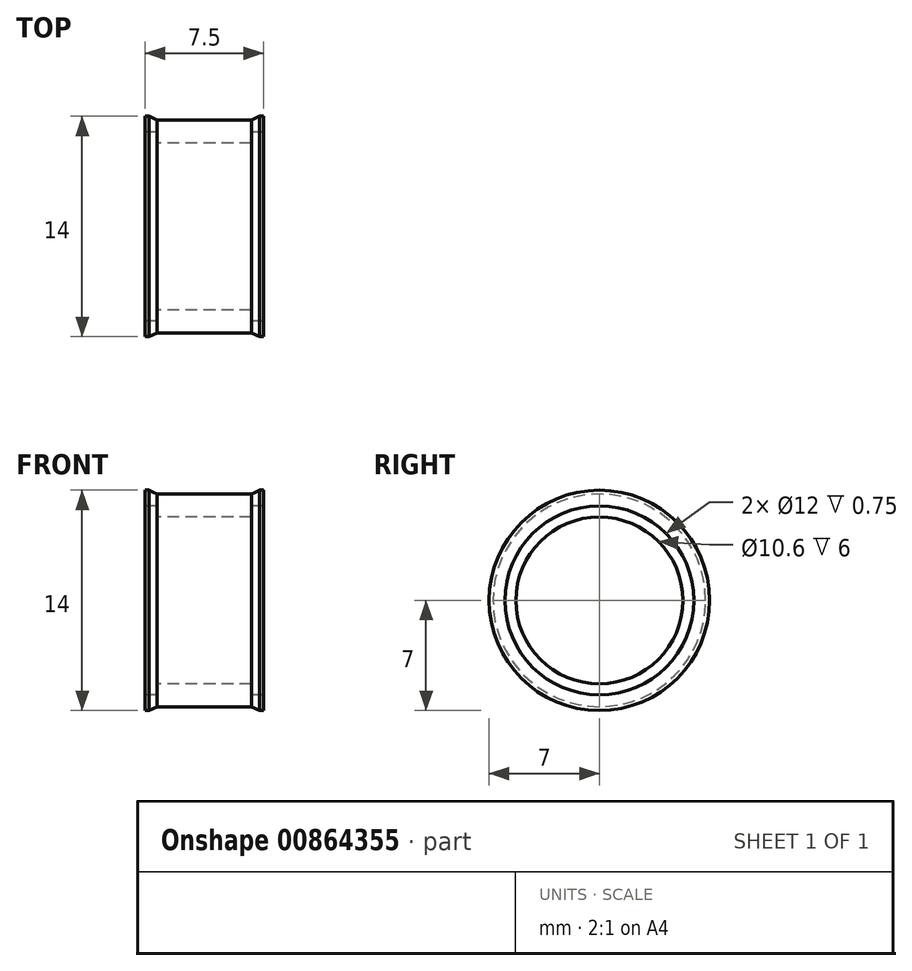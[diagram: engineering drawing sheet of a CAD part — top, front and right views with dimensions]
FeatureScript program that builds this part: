
annotation { "Feature Type Name" : "Feature", "Feature Type Description" : "" }
export const myFeature = defineFeature(function(context is Context, id is Id, definition is map)
    precondition{}
    {
        {
            var Q0;
            Q0=qCreatedBy(makeId("Front.planeOp"),FACE);
            var sketch = newSketch(context, id + "F0", { "sketchPlane" : qUnion([Q0])});
            skLineSegment(sketch, "E0", {"start": v(-1.64, 0) * mm, "end": v(11.73, 0) * mm, "construction": true});
            skLineSegment(sketch, "E1", {"start": v(0, 7) * mm, "end": v(0, 6) * mm});
            skLineSegment(sketch, "E2", {"start": v(0.75, 5.3) * mm, "end": v(6.75, 5.3) * mm});
            skLineSegment(sketch, "E3", {"start": v(7.5, 6) * mm, "end": v(7.5, 7) * mm});
            skLineSegment(sketch, "E4", {"start": v(7.5, 7) * mm, "end": v(7.25, 7) * mm});
            skLineSegment(sketch, "E5", {"start": v(7.25, 7) * mm, "end": v(6.75, 6.75) * mm});
            skLineSegment(sketch, "E6", {"start": v(6.75, 6.75) * mm, "end": v(0.75, 6.75) * mm});
            skLineSegment(sketch, "E7", {"start": v(0.75, 6.75) * mm, "end": v(0.25, 7) * mm});
            skLineSegment(sketch, "E8", {"start": v(0.25, 7) * mm, "end": v(0, 7) * mm});
            skLineSegment(sketch, "E9", {"start": v(0, 6) * mm, "end": v(0.75, 6) * mm});
            skLineSegment(sketch, "E10", {"start": v(0.75, 6) * mm, "end": v(0.75, 5.3) * mm});
            skLineSegment(sketch, "E11", {"start": v(6.75, 5.3) * mm, "end": v(6.75, 6) * mm});
            skLineSegment(sketch, "E12", {"start": v(6.75, 6) * mm, "end": v(7.5, 6) * mm});
            skSolve(sketch);
        }
        {
            var Q0;
            Q0 = qSketchRegion(id + "F0", true);
            var Q1;
            Q1=sQuery(id+"F0.wireOp",EDGE,"E0");
            revolve(context, id + "F1", {"surfaceOperationType" : NewSurfaceOperationType.NEW, "entities" : qUnion([Q0]), "axis" : qUnion([Q1]), "revolveType" : RevolveType.FULL});
        }
    });
